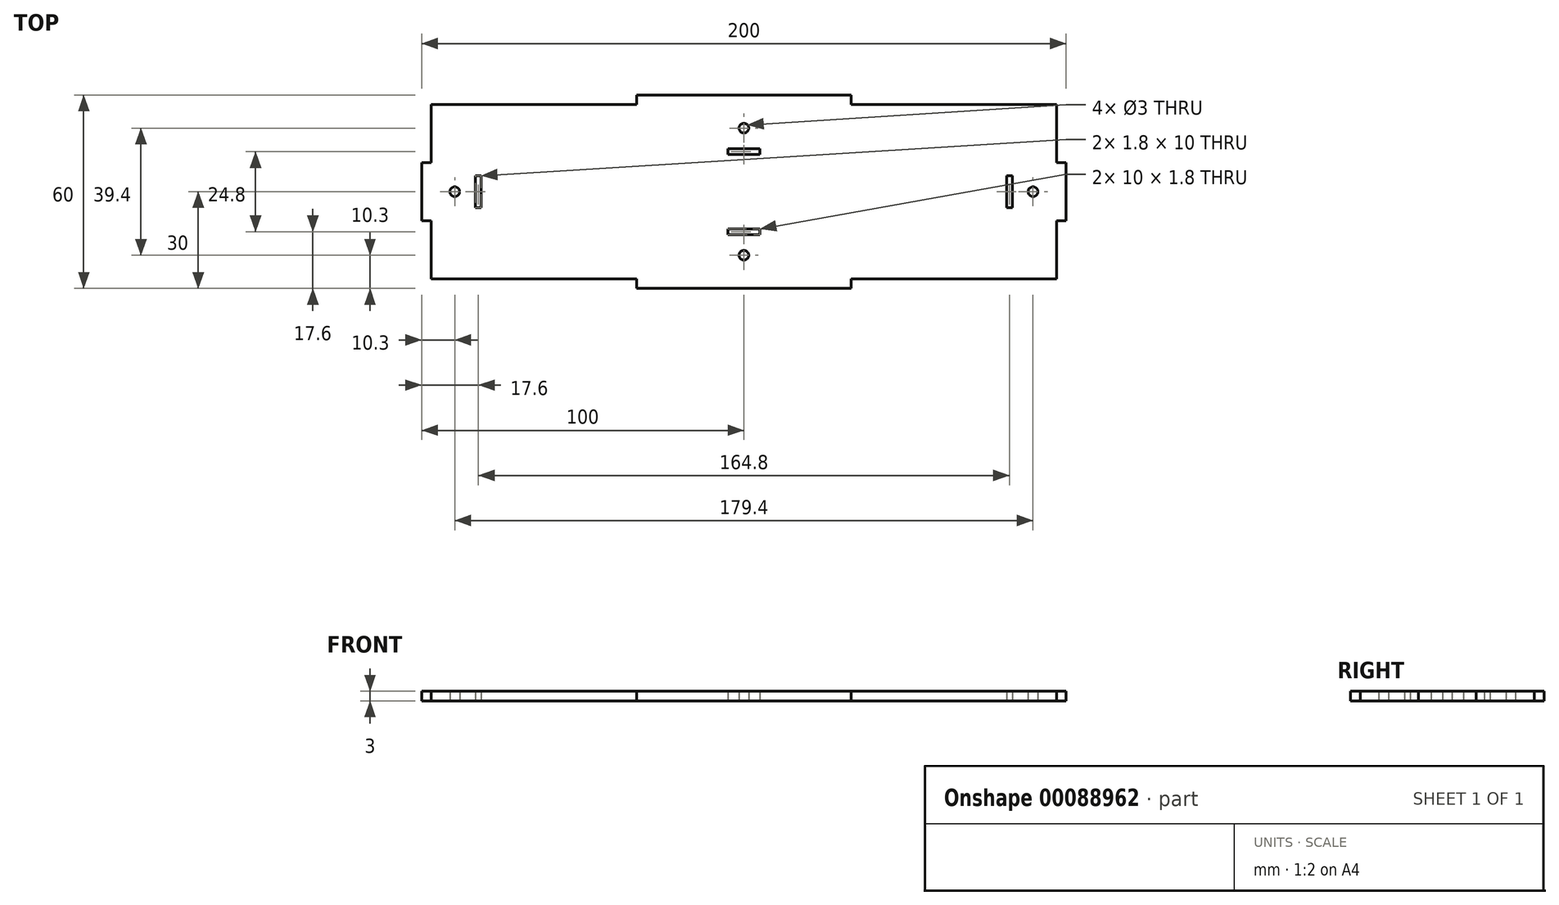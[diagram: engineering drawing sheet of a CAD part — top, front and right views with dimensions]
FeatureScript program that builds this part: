
annotation { "Feature Type Name" : "Feature", "Feature Type Description" : "" }
export const myFeature = defineFeature(function(context is Context, id is Id, definition is map)
    precondition{}
    {
        {
            var Q0;
            Q0=qCreatedBy(makeId("Top.planeOp"),FACE);
            var sketch = newSketch(context, id + "F0", { "sketchPlane" : qUnion([Q0])});
            skLineSegment(sketch, "E0.bottom", {"start": v(-97, 27) * mm, "end": v(-33.33, 27) * mm});
            skLineSegment(sketch, "E0.top", {"start": v(-97, -27) * mm, "end": v(-33.33, -27) * mm});
            skLineSegment(sketch, "E0.left", {"start": v(-97, 27) * mm, "end": v(-97, 9) * mm});
            skLineSegment(sketch, "E0.right", {"start": v(97, 27) * mm, "end": v(97, 9) * mm});
            skLineSegment(sketch, "E1.bottom", {"start": v(-97, 9) * mm, "end": v(-100, 9) * mm});
            skLineSegment(sketch, "E1.top", {"start": v(-97, -9) * mm, "end": v(-100, -9) * mm});
            skLineSegment(sketch, "E1.right", {"start": v(-100, 9) * mm, "end": v(-100, -9) * mm});
            skLineSegment(sketch, "E2.top", {"start": v(-33.33, 30) * mm, "end": v(33.33, 30) * mm});
            skLineSegment(sketch, "E2.left", {"start": v(-33.33, 27) * mm, "end": v(-33.33, 30) * mm});
            skLineSegment(sketch, "E2.right", {"start": v(33.33, 27) * mm, "end": v(33.33, 30) * mm});
            skLineSegment(sketch, "E3.bottom", {"start": v(97, 9) * mm, "end": v(100, 9) * mm});
            skLineSegment(sketch, "E3.top", {"start": v(97, -9) * mm, "end": v(100, -9) * mm});
            skLineSegment(sketch, "E3.right", {"start": v(100, 9) * mm, "end": v(100, -9) * mm});
            skLineSegment(sketch, "E4.top", {"start": v(33.33, -30) * mm, "end": v(-33.33, -30) * mm});
            skLineSegment(sketch, "E4.left", {"start": v(33.33, -27) * mm, "end": v(33.33, -30) * mm});
            skLineSegment(sketch, "E4.right", {"start": v(-33.33, -27) * mm, "end": v(-33.33, -30) * mm});
            skLineSegment(sketch, "E5.trimOffspring", {"start": v(33.33, 27) * mm, "end": v(97, 27) * mm});
            skLineSegment(sketch, "E6.trimOffspring", {"start": v(33.33, -27) * mm, "end": v(97, -27) * mm});
            skLineSegment(sketch, "E7.trimOffspring", {"start": v(-97, -9) * mm, "end": v(-97, -27) * mm});
            skLineSegment(sketch, "E8.trimOffspring", {"start": v(97, -9) * mm, "end": v(97, -27) * mm});
            skLineSegment(sketch, "E9", {"start": v(-100, 30) * mm, "end": v(-33.33, 30) * mm, "construction": true});
            skLineSegment(sketch, "E10", {"start": v(33.33, 30) * mm, "end": v(100, 30) * mm, "construction": true});
            skCircle(sketch, "E11", {"center": v(-89.7, 0) * mm, "radius": 1.5 * mm});
            skLineSegment(sketch, "E12.bottom", {"start": v(-83.3, 5) * mm, "end": v(-81.5, 5) * mm});
            skLineSegment(sketch, "E12.top", {"start": v(-83.3, -5) * mm, "end": v(-81.5, -5) * mm});
            skLineSegment(sketch, "E12.left", {"start": v(-83.3, 5) * mm, "end": v(-83.3, -5) * mm});
            skLineSegment(sketch, "E12.right", {"start": v(-81.5, 5) * mm, "end": v(-81.5, -5) * mm});
            skLineSegment(sketch, "E13.MirrorCS", {"start": v(83.3, 5) * mm, "end": v(81.5, 5) * mm});
            skLineSegment(sketch, "E14.MirrorCS", {"start": v(83.3, -5) * mm, "end": v(81.5, -5) * mm});
            skLineSegment(sketch, "E15.MirrorCS", {"start": v(81.5, 5) * mm, "end": v(81.5, -5) * mm});
            skLineSegment(sketch, "E16.MirrorCS", {"start": v(83.3, 5) * mm, "end": v(83.3, -5) * mm});
            skCircle(sketch, "E17.MirrorC", {"center": v(89.7, 0) * mm, "radius": 1.5 * mm});
            skCircle(sketch, "E18", {"center": v(0, 19.7) * mm, "radius": 1.5 * mm});
            skLineSegment(sketch, "E19.bottom", {"start": v(5, 13.3) * mm, "end": v(-5, 13.3) * mm});
            skLineSegment(sketch, "E19.top", {"start": v(5, 11.5) * mm, "end": v(-5, 11.5) * mm});
            skLineSegment(sketch, "E19.left", {"start": v(5, 13.3) * mm, "end": v(5, 11.5) * mm});
            skLineSegment(sketch, "E19.right", {"start": v(-5, 13.3) * mm, "end": v(-5, 11.5) * mm});
            skLineSegment(sketch, "E20.MirrorCS", {"start": v(-5, -13.3) * mm, "end": v(-5, -11.5) * mm});
            skLineSegment(sketch, "E21.MirrorCS", {"start": v(5, -13.3) * mm, "end": v(5, -11.5) * mm});
            skCircle(sketch, "E22.MirrorC", {"center": v(0, -19.7) * mm, "radius": 1.5 * mm});
            skLineSegment(sketch, "E23.MirrorCS", {"start": v(5, -11.5) * mm, "end": v(-5, -11.5) * mm});
            skLineSegment(sketch, "E24.MirrorCS", {"start": v(5, -13.3) * mm, "end": v(-5, -13.3) * mm});
            skSolve(sketch);
        }
        {
            var Q0;
            Q0 = qSketchRegion(id + "F0", true);
            extrude(context, id + "F1", {"entities" : qUnion([Q0]), "depth" : 3 * mm});
        }
    });
